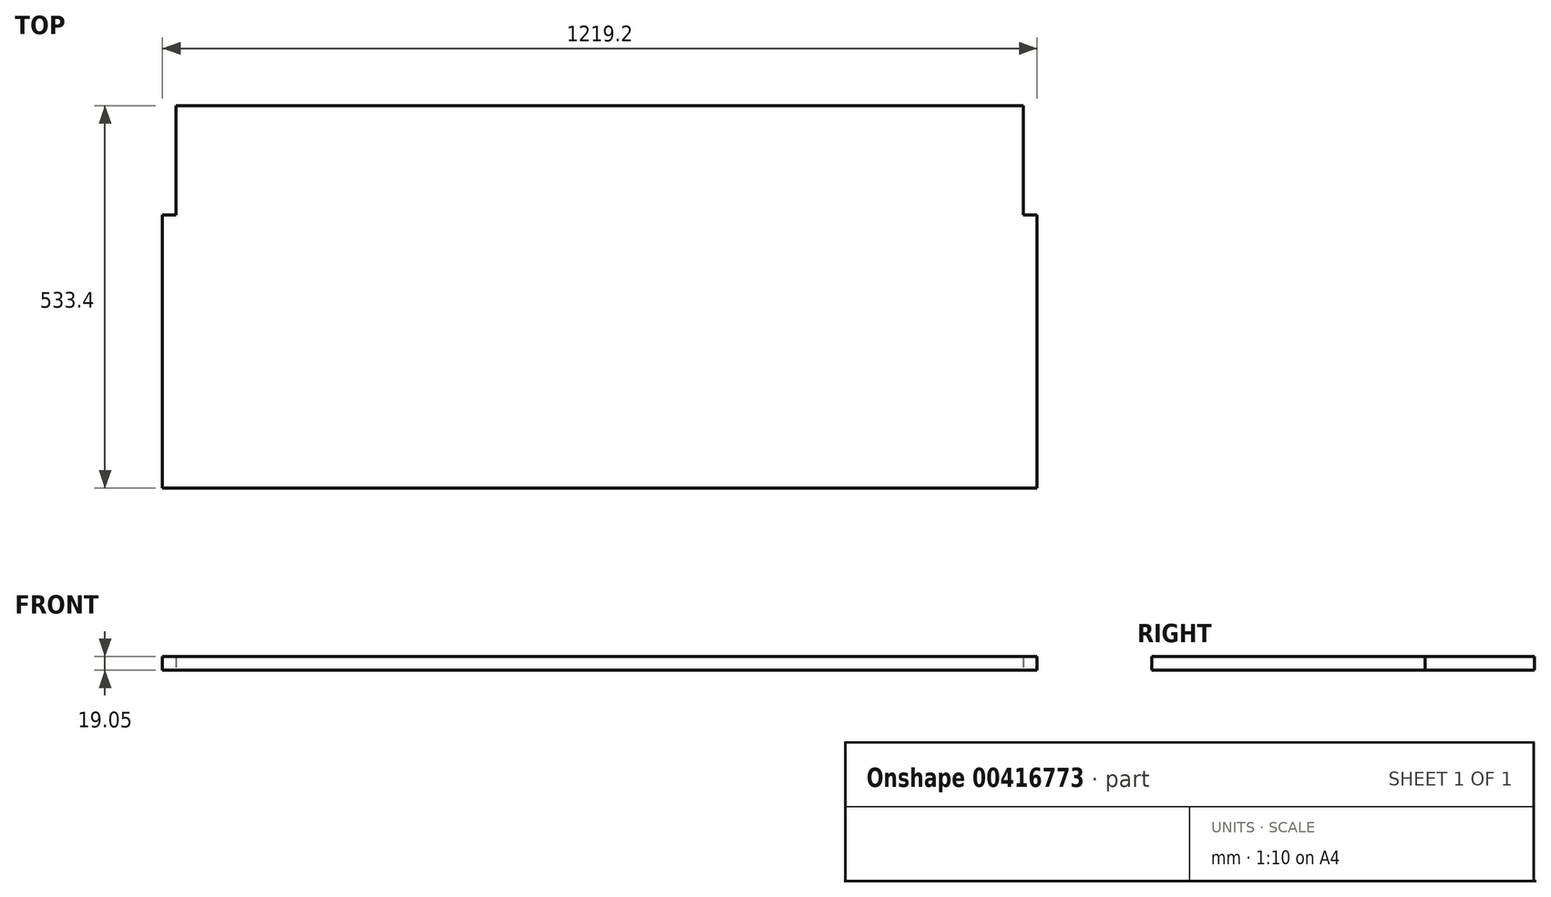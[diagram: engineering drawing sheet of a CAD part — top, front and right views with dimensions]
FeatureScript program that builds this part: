
annotation { "Feature Type Name" : "Feature", "Feature Type Description" : "" }
export const myFeature = defineFeature(function(context is Context, id is Id, definition is map)
    precondition{}
    {
        {
            var Q0;
            Q0=qCreatedBy(makeId("Top.planeOp"),FACE);
            var sketch = newSketch(context, id + "F0", { "sketchPlane" : qUnion([Q0])});
            skLineSegment(sketch, "E0", {"start": v(0, 0) * mm, "end": v(1219.2, 0) * mm});
            skLineSegment(sketch, "E1", {"start": v(1219.2, 0) * mm, "end": v(1219.2, 381) * mm});
            skLineSegment(sketch, "E2", {"start": v(1219.2, 381) * mm, "end": v(1200.15, 381) * mm});
            skLineSegment(sketch, "E3", {"start": v(1200.15, 381) * mm, "end": v(1200.15, 533.4) * mm});
            skLineSegment(sketch, "E4", {"start": v(1200.15, 533.4) * mm, "end": v(19.05, 533.4) * mm});
            skLineSegment(sketch, "E5", {"start": v(19.05, 533.4) * mm, "end": v(19.05, 381) * mm});
            skLineSegment(sketch, "E6", {"start": v(19.05, 381) * mm, "end": v(0, 381) * mm});
            skLineSegment(sketch, "E7", {"start": v(0, 381) * mm, "end": v(0, 0) * mm});
            skSolve(sketch);
        }
        {
            var Q0;
            Q0 = qSketchRegion(id + "F0", true);
            extrude(context, id + "F1", {"entities" : qUnion([Q0]), "depth" : 19.05 * mm});
        }
    });
